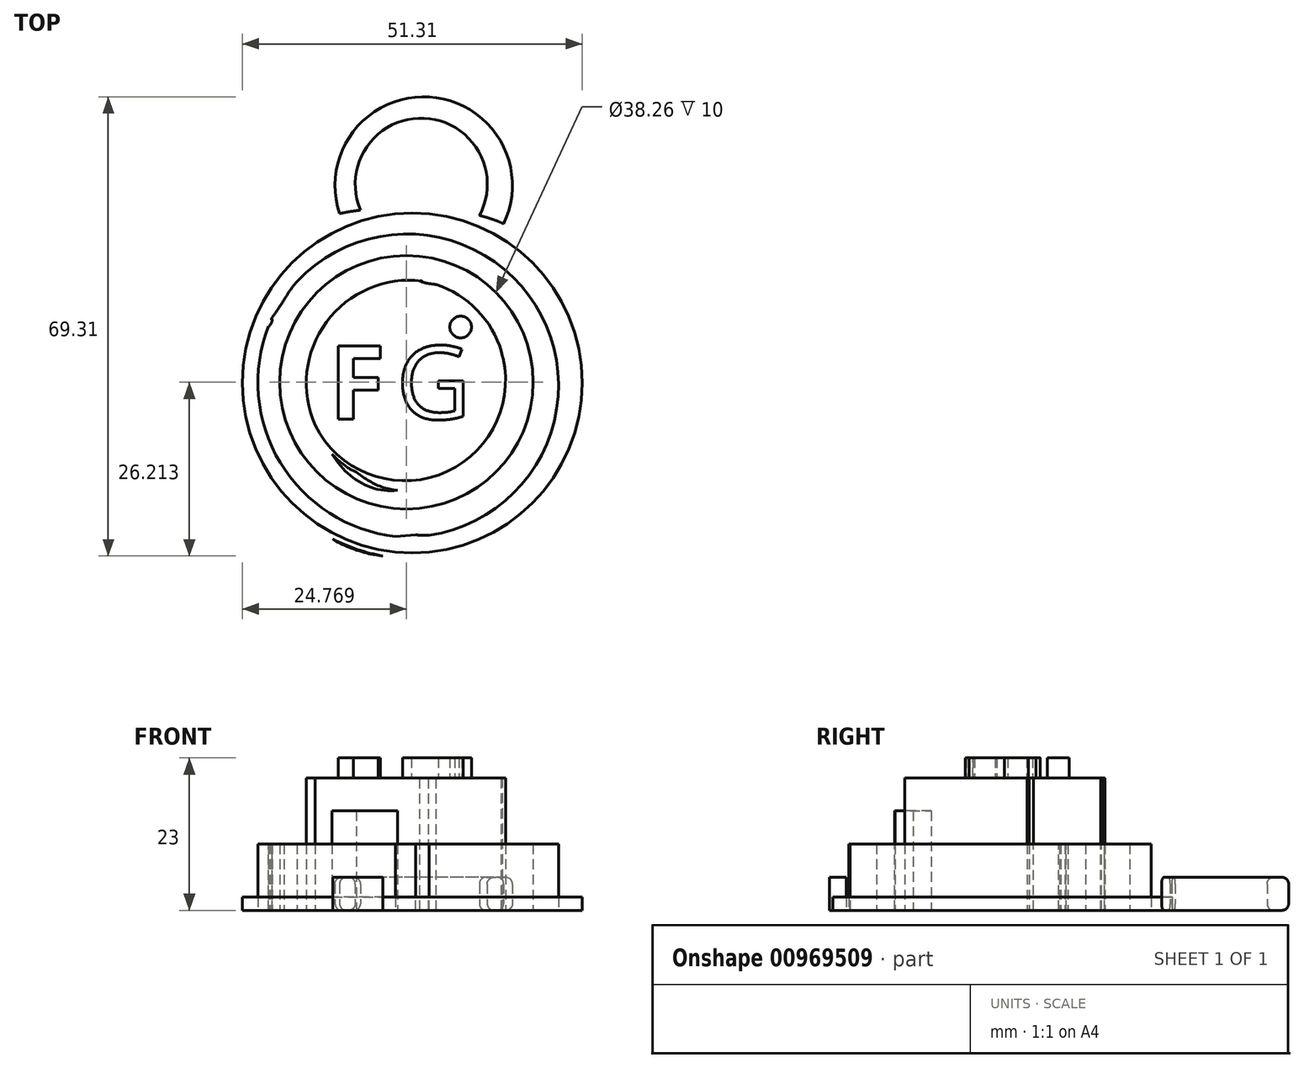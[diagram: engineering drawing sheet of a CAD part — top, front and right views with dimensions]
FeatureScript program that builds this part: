
annotation { "Feature Type Name" : "Feature", "Feature Type Description" : "" }
export const myFeature = defineFeature(function(context is Context, id is Id, definition is map)
    precondition{}
    {
        {
            var Q0;
            Q0=qCreatedBy(makeId("Top.planeOp"),FACE);
            var sketch = newSketch(context, id + "F0", { "sketchPlane" : qUnion([Q0])});
            skLineSegment(sketch, "E0", {"start": v(-44.03, -23.25) * mm, "end": v(-47.07, -23.48) * mm});
            skLineSegment(sketch, "E1", {"start": v(-47.07, -23.48) * mm, "end": v(-43.76, -23.38) * mm});
            skLineSegment(sketch, "E2", {"start": v(-0.42, -4.93) * mm, "end": v(0.75, -6.1) * mm});
            skLineSegment(sketch, "E3", {"start": v(0.75, -6.1) * mm, "end": v(0.2, -6.66) * mm});
            skLineSegment(sketch, "E4", {"start": v(0.2, -6.66) * mm, "end": v(-0.35, -7.2) * mm});
            skLineSegment(sketch, "E5", {"start": v(-0.35, -7.2) * mm, "end": v(-1.3, -6.23) * mm});
            skLineSegment(sketch, "E6", {"start": v(-5.27, -11.6) * mm, "end": v(-5.27, -10.95) * mm});
            skLineSegment(sketch, "E7", {"start": v(-5.27, -10.95) * mm, "end": v(-1.83, -10.95) * mm});
            skLineSegment(sketch, "E8", {"start": v(-1.83, -10.95) * mm, "end": v(1.61, -10.95) * mm});
            skLineSegment(sketch, "E9", {"start": v(1.61, -10.95) * mm, "end": v(1.53, -12.4) * mm});
            skLineSegment(sketch, "E10", {"start": v(34.95, -9.23) * mm, "end": v(34.95, -3.27) * mm});
            skLineSegment(sketch, "E11", {"start": v(34.95, -3.27) * mm, "end": v(35.66, -3.2) * mm});
            skLineSegment(sketch, "E12", {"start": v(35.66, -3.2) * mm, "end": v(36.37, -3.1) * mm});
            skLineSegment(sketch, "E13", {"start": v(36.37, -3.1) * mm, "end": v(36.45, -9.14) * mm});
            skLineSegment(sketch, "E14", {"start": v(44.6, -9.4) * mm, "end": v(44.74, -3.27) * mm});
            skLineSegment(sketch, "E15", {"start": v(44.74, -3.27) * mm, "end": v(45.47, -3.19) * mm});
            skLineSegment(sketch, "E16", {"start": v(45.47, -3.19) * mm, "end": v(46.2, -3.1) * mm});
            skLineSegment(sketch, "E17", {"start": v(46.2, -3.1) * mm, "end": v(46.18, -9.01) * mm});
            skLineSegment(sketch, "E18", {"start": v(4.45, -10.68) * mm, "end": v(4.52, -3.27) * mm});
            skLineSegment(sketch, "E19", {"start": v(4.52, -3.27) * mm, "end": v(5.85, -3.19) * mm});
            skLineSegment(sketch, "E20", {"start": v(9.42, -11.31) * mm, "end": v(8.63, -11.48) * mm});
            skLineSegment(sketch, "E21", {"start": v(8.63, -11.48) * mm, "end": v(11.3, -15.05) * mm});
            skLineSegment(sketch, "E22", {"start": v(11.3, -15.05) * mm, "end": v(13.95, -18.62) * mm});
            skLineSegment(sketch, "E23", {"start": v(13.95, -18.62) * mm, "end": v(13.08, -18.7) * mm});
            skLineSegment(sketch, "E24", {"start": v(5.98, -15.05) * mm, "end": v(5.98, -18.75) * mm});
            skLineSegment(sketch, "E25", {"start": v(5.98, -18.75) * mm, "end": v(5.3, -18.75) * mm});
            skLineSegment(sketch, "E26", {"start": v(7.18, -4.46) * mm, "end": v(5.98, -4.46) * mm});
            skLineSegment(sketch, "E27", {"start": v(5.98, -4.46) * mm, "end": v(5.98, -7.27) * mm});
            skLineSegment(sketch, "E28", {"start": v(5.98, -7.27) * mm, "end": v(5.98, -10.08) * mm});
            skLineSegment(sketch, "E29", {"start": v(5.98, -10.08) * mm, "end": v(7.86, -9.97) * mm});
            skLineSegment(sketch, "E30", {"start": v(49.96, -11.01) * mm, "end": v(50.03, -3.27) * mm});
            skLineSegment(sketch, "E31", {"start": v(50.03, -3.27) * mm, "end": v(51.62, -3.19) * mm});
            skLineSegment(sketch, "E32", {"start": v(52.88, -11.87) * mm, "end": v(51.49, -11.87) * mm});
            skLineSegment(sketch, "E33", {"start": v(51.49, -11.87) * mm, "end": v(51.49, -15.31) * mm});
            skLineSegment(sketch, "E34", {"start": v(51.49, -15.31) * mm, "end": v(51.49, -18.75) * mm});
            skLineSegment(sketch, "E35", {"start": v(51.49, -18.75) * mm, "end": v(50.69, -18.75) * mm});
            skLineSegment(sketch, "E36", {"start": v(50.69, -18.75) * mm, "end": v(49.9, -18.75) * mm});
            skLineSegment(sketch, "E37", {"start": v(49.9, -18.75) * mm, "end": v(49.96, -11.01) * mm});
            skLineSegment(sketch, "E38", {"start": v(52.61, -4.47) * mm, "end": v(51.49, -4.46) * mm});
            skLineSegment(sketch, "E39", {"start": v(51.49, -4.46) * mm, "end": v(51.49, -7.5) * mm});
            skLineSegment(sketch, "E40", {"start": v(-2.62, 13.4) * mm, "end": v(-2.62, 19.22) * mm});
            skLineSegment(sketch, "E41", {"start": v(-2.62, 19.22) * mm, "end": v(-1.38, 19.3) * mm});
            skLineSegment(sketch, "E42", {"start": v(-1.38, 19.3) * mm, "end": v(-0.14, 19.38) * mm});
            skLineSegment(sketch, "E43", {"start": v(-0.14, 19.38) * mm, "end": v(-0.06, 13.74) * mm});
            skLineSegment(sketch, "E44", {"start": v(7.57, 13.53) * mm, "end": v(7.7, 19.22) * mm});
            skLineSegment(sketch, "E45", {"start": v(7.7, 19.22) * mm, "end": v(8.89, 19.22) * mm});
            skLineSegment(sketch, "E46", {"start": v(8.89, 19.22) * mm, "end": v(10.08, 19.22) * mm});
            skLineSegment(sketch, "E47", {"start": v(10.08, 19.22) * mm, "end": v(10.08, 13.4) * mm});
            skLineSegment(sketch, "E48", {"start": v(1.1, 3.6) * mm, "end": v(1.1, 3.6) * mm});
            skLineSegment(sketch, "E49", {"start": v(22.7, 13.81) * mm, "end": v(22.78, 19.22) * mm});
            skLineSegment(sketch, "E50", {"start": v(22.78, 19.22) * mm, "end": v(23.97, 19.22) * mm});
            skLineSegment(sketch, "E51", {"start": v(23.97, 19.22) * mm, "end": v(25.16, 19.22) * mm});
            skLineSegment(sketch, "E52", {"start": v(25.16, 19.22) * mm, "end": v(25.3, 13.53) * mm});
            skLineSegment(sketch, "E53", {"start": v(32.92, 13.86) * mm, "end": v(33.01, 19.35) * mm});
            skLineSegment(sketch, "E54", {"start": v(33.01, 19.35) * mm, "end": v(34.18, 19.35) * mm});
            skLineSegment(sketch, "E55", {"start": v(34.18, 19.35) * mm, "end": v(35.35, 19.35) * mm});
            skLineSegment(sketch, "E56", {"start": v(35.35, 19.35) * mm, "end": v(35.35, 13.32) * mm});
            skLineSegment(sketch, "E57", {"start": v(-13.27, 11.48) * mm, "end": v(-13.2, 19.22) * mm});
            skLineSegment(sketch, "E58", {"start": v(-13.2, 19.22) * mm, "end": v(-8.97, 19.22) * mm});
            skLineSegment(sketch, "E59", {"start": v(-8.97, 19.22) * mm, "end": v(-4.74, 19.22) * mm});
            skLineSegment(sketch, "E60", {"start": v(-4.74, 19.22) * mm, "end": v(-4.66, 18.1) * mm});
            skLineSegment(sketch, "E61", {"start": v(-4.66, 18.1) * mm, "end": v(-4.57, 16.97) * mm});
            skLineSegment(sketch, "E62", {"start": v(-4.57, 16.97) * mm, "end": v(-7.63, 16.97) * mm});
            skLineSegment(sketch, "E63", {"start": v(-7.63, 16.97) * mm, "end": v(-10.69, 16.97) * mm});
            skLineSegment(sketch, "E64", {"start": v(-10.69, 16.97) * mm, "end": v(-10.69, 15.12) * mm});
            skLineSegment(sketch, "E65", {"start": v(-10.69, 15.12) * mm, "end": v(-10.69, 13.26) * mm});
            skLineSegment(sketch, "E66", {"start": v(-10.69, 13.26) * mm, "end": v(-7.65, 13.26) * mm});
            skLineSegment(sketch, "E67", {"start": v(-7.65, 13.26) * mm, "end": v(-4.6, 13.26) * mm});
            skLineSegment(sketch, "E68", {"start": v(-4.6, 13.26) * mm, "end": v(-4.6, 12.07) * mm});
            skLineSegment(sketch, "E69", {"start": v(-4.6, 12.07) * mm, "end": v(-4.6, 10.88) * mm});
            skLineSegment(sketch, "E70", {"start": v(-4.6, 10.88) * mm, "end": v(-7.65, 10.88) * mm});
            skLineSegment(sketch, "E71", {"start": v(-7.65, 10.88) * mm, "end": v(-10.69, 10.88) * mm});
            skLineSegment(sketch, "E72", {"start": v(-10.69, 10.88) * mm, "end": v(-10.69, 7.31) * mm});
            skLineSegment(sketch, "E73", {"start": v(-10.69, 7.31) * mm, "end": v(-10.69, 3.74) * mm});
            skLineSegment(sketch, "E74", {"start": v(-10.69, 3.74) * mm, "end": v(-12.02, 3.74) * mm});
            skLineSegment(sketch, "E75", {"start": v(-12.02, 3.74) * mm, "end": v(-13.34, 3.74) * mm});
            skLineSegment(sketch, "E76", {"start": v(-13.34, 3.74) * mm, "end": v(-13.27, 11.48) * mm});
            skLineSegment(sketch, "E77", {"start": v(14.99, 10.29) * mm, "end": v(15.01, 16.84) * mm});
            skLineSegment(sketch, "E78", {"start": v(15.01, 16.84) * mm, "end": v(13, 16.91) * mm});
            skLineSegment(sketch, "E79", {"start": v(13, 16.91) * mm, "end": v(10.98, 17) * mm});
            skLineSegment(sketch, "E80", {"start": v(10.98, 17) * mm, "end": v(11.06, 18.1) * mm});
            skLineSegment(sketch, "E81", {"start": v(11.06, 18.1) * mm, "end": v(11.14, 19.22) * mm});
            skLineSegment(sketch, "E82", {"start": v(11.14, 19.22) * mm, "end": v(16.43, 19.22) * mm});
            skLineSegment(sketch, "E83", {"start": v(16.43, 19.22) * mm, "end": v(21.72, 19.22) * mm});
            skLineSegment(sketch, "E84", {"start": v(21.72, 19.22) * mm, "end": v(21.8, 18.1) * mm});
            skLineSegment(sketch, "E85", {"start": v(21.8, 18.1) * mm, "end": v(21.88, 17) * mm});
            skLineSegment(sketch, "E86", {"start": v(21.88, 17) * mm, "end": v(19.82, 16.91) * mm});
            skLineSegment(sketch, "E87", {"start": v(19.82, 16.91) * mm, "end": v(17.75, 16.84) * mm});
            skLineSegment(sketch, "E88", {"start": v(17.75, 16.84) * mm, "end": v(17.75, 10.29) * mm});
            skLineSegment(sketch, "E89", {"start": v(17.75, 10.29) * mm, "end": v(17.75, 3.74) * mm});
            skLineSegment(sketch, "E90", {"start": v(17.75, 3.74) * mm, "end": v(16.36, 3.74) * mm});
            skLineSegment(sketch, "E91", {"start": v(16.36, 3.74) * mm, "end": v(14.96, 3.74) * mm});
            skLineSegment(sketch, "E92", {"start": v(14.96, 3.74) * mm, "end": v(14.99, 10.29) * mm});
            skLineSegment(sketch, "E93", {"start": v(38.06, 11.48) * mm, "end": v(38.13, 19.22) * mm});
            skLineSegment(sketch, "E94", {"start": v(38.13, 19.22) * mm, "end": v(41.1, 19.18) * mm});
            skLineSegment(sketch, "E95", {"start": v(44.73, 11.04) * mm, "end": v(43.66, 10.55) * mm});
            skLineSegment(sketch, "E96", {"start": v(43.66, 10.55) * mm, "end": v(46.05, 7.29) * mm});
            skLineSegment(sketch, "E97", {"start": v(63.29, 4.6) * mm, "end": v(63.67, 3.74) * mm});
            skLineSegment(sketch, "E98", {"start": v(63.67, 3.74) * mm, "end": v(62.27, 3.74) * mm});
            skLineSegment(sketch, "E99", {"start": v(62.27, 3.74) * mm, "end": v(60.88, 3.74) * mm});
            skLineSegment(sketch, "E100", {"start": v(60.88, 3.74) * mm, "end": v(60.06, 5.66) * mm});
            skLineSegment(sketch, "E101", {"start": v(60.06, 5.66) * mm, "end": v(59.24, 7.57) * mm});
            skLineSegment(sketch, "E102", {"start": v(59.24, 7.57) * mm, "end": v(56.22, 7.57) * mm});
            skLineSegment(sketch, "E103", {"start": v(56.22, 7.57) * mm, "end": v(53.2, 7.57) * mm});
            skLineSegment(sketch, "E104", {"start": v(53.2, 7.57) * mm, "end": v(52.75, 6.66) * mm});
            skLineSegment(sketch, "E105", {"start": v(51.9, 4.74) * mm, "end": v(51.5, 3.74) * mm});
            skLineSegment(sketch, "E106", {"start": v(51.5, 3.74) * mm, "end": v(48.6, 3.74) * mm});
            skLineSegment(sketch, "E107", {"start": v(48.6, 3.74) * mm, "end": v(45.7, 3.74) * mm});
            skLineSegment(sketch, "E108", {"start": v(45.7, 3.74) * mm, "end": v(43.43, 6.9) * mm});
            skLineSegment(sketch, "E109", {"start": v(40.64, 7.06) * mm, "end": v(40.64, 3.74) * mm});
            skLineSegment(sketch, "E110", {"start": v(40.64, 3.74) * mm, "end": v(39.31, 3.74) * mm});
            skLineSegment(sketch, "E111", {"start": v(39.31, 3.74) * mm, "end": v(37.99, 3.74) * mm});
            skLineSegment(sketch, "E112", {"start": v(37.99, 3.74) * mm, "end": v(38.06, 11.48) * mm});
            skLineSegment(sketch, "E113", {"start": v(42.1, 16.79) * mm, "end": v(40.77, 16.84) * mm});
            skLineSegment(sketch, "E114", {"start": v(40.77, 16.84) * mm, "end": v(40.7, 14.78) * mm});
            skLineSegment(sketch, "E115", {"start": v(40.7, 14.78) * mm, "end": v(40.62, 12.73) * mm});
            skLineSegment(sketch, "E116", {"start": v(40.62, 12.73) * mm, "end": v(41.95, 12.73) * mm});
            skFitSpline(sketch, "E117", {"points": [v(-48.97, -26.41) * mm, v(-51.63, -25.94) * mm, v(-55.3, -24.57) * mm, v(-57.59, -23.21) * mm]});
            skFitSpline(sketch, "E118", {"points": [v(-57.59, -23.21) * mm, v(-63.3, -19.81) * mm, v(-66.86, -15.56) * mm, v(-69.4, -9.15) * mm]});
            skFitSpline(sketch, "E119", {"points": [v(-69.4, -9.15) * mm, v(-71.48, -3.92) * mm, v(-71.54, 3.34) * mm, v(-69.55, 8.65) * mm]});
            skFitSpline(sketch, "E120", {"points": [v(-69.56, 8.67) * mm, v(-66.12, 17.83) * mm, v(-58.94, 24.16) * mm, v(-49.87, 26.04) * mm]});
            skFitSpline(sketch, "E121", {"points": [v(-49.86, 26.02) * mm, v(-46.19, 26.78) * mm, v(-40.37, 26.59) * mm, v(-37.07, 25.6) * mm]});
            skFitSpline(sketch, "E122", {"points": [v(-37.07, 25.6) * mm, v(-30.64, 23.67) * mm, v(-25.03, 19.32) * mm, v(-21.64, 13.64) * mm]});
            skFitSpline(sketch, "E123", {"points": [v(-21.64, 13.64) * mm, v(-17.98, 7.51) * mm, v(-16.93, 0.08) * mm, v(-18.72, -6.9) * mm]});
            skFitSpline(sketch, "E124", {"points": [v(-18.72, -6.9) * mm, v(-21.07, -16.02) * mm, v(-28.59, -23.55) * mm, v(-37.68, -25.92) * mm]});
            skFitSpline(sketch, "E125", {"points": [v(-37.68, -25.92) * mm, v(-40.2, -26.57) * mm, v(-46.51, -26.85) * mm, v(-48.97, -26.41) * mm]});
            skFitSpline(sketch, "E126", {"points": [v(-38.2, -22.63) * mm, v(-35.14, -21.72) * mm, v(-33.7, -21.08) * mm, v(-31.51, -19.6) * mm]});
            skFitSpline(sketch, "E127", {"points": [v(-31.51, -19.6) * mm, v(-26.64, -16.35) * mm, v(-23.18, -11.38) * mm, v(-21.75, -5.6) * mm]});
            skFitSpline(sketch, "E128", {"points": [v(-21.75, -5.6) * mm, v(-20.9, -2.13) * mm, v(-20.94, 2.46) * mm, v(-21.88, 5.9) * mm]});
            skFitSpline(sketch, "E129", {"points": [v(-21.88, 5.9) * mm, v(-23.68, 12.54) * mm, v(-28.15, 18.04) * mm, v(-34.12, 20.95) * mm]});
            skFitSpline(sketch, "E130", {"points": [v(-34.12, 20.95) * mm, v(-39.89, 23.76) * mm, v(-46.96, 24.05) * mm, v(-53.02, 21.71) * mm]});
            skFitSpline(sketch, "E131", {"points": [v(-53.02, 21.71) * mm, v(-57.82, 19.87) * mm, v(-62.76, 15.41) * mm, v(-65.06, 10.88) * mm]});
            skFitSpline(sketch, "E132", {"points": [v(-65.06, 10.88) * mm, v(-65.7, 9.62) * mm, v(-65.47, 9.88) * mm, v(-63.9, 12.23) * mm]});
            skFitSpline(sketch, "E133", {"points": [v(-63.9, 12.23) * mm, v(-62.4, 14.5) * mm, v(-59.48, 17.39) * mm, v(-57.14, 18.93) * mm]});
            skFitSpline(sketch, "E134", {"points": [v(-57.14, 18.93) * mm, v(-55.36, 20.11) * mm, v(-52.56, 21.26) * mm, v(-49.92, 21.9) * mm]});
            skFitSpline(sketch, "E135", {"points": [v(-49.92, 21.9) * mm, v(-47.26, 22.55) * mm, v(-42.13, 22.48) * mm, v(-39.4, 21.75) * mm]});
            skFitSpline(sketch, "E136", {"points": [v(-39.4, 21.75) * mm, v(-31.8, 19.74) * mm, v(-25.84, 14.14) * mm, v(-23.33, 6.65) * mm]});
            skFitSpline(sketch, "E137", {"points": [v(-23.33, 6.65) * mm, v(-22.52, 4.24) * mm, v(-22.49, 3.96) * mm, v(-22.48, -0.23) * mm]});
            skFitSpline(sketch, "E138", {"points": [v(-22.48, -0.23) * mm, v(-22.46, -5.24) * mm, v(-22.86, -7.13) * mm, v(-24.7, -10.8) * mm]});
            skFitSpline(sketch, "E139", {"points": [v(-24.7, -10.8) * mm, v(-28.37, -18.09) * mm, v(-35.4, -22.62) * mm, v(-44.03, -23.25) * mm]});
            skFitSpline(sketch, "E140", {"points": [v(-43.76, -23.38) * mm, v(-41.2, -23.31) * mm, v(-39.94, -23.14) * mm, v(-38.2, -22.63) * mm]});
            skFitSpline(sketch, "E141", {"points": [v(-41.15, -15.54) * mm, v(-37.63, -14.7) * mm, v(-33.69, -11.85) * mm, v(-31.89, -8.86) * mm]});
            skFitSpline(sketch, "E142", {"points": [v(-31.89, -8.86) * mm, v(-30.14, -5.94) * mm, v(-29.65, -4.17) * mm, v(-29.63, -0.63) * mm]});
            skFitSpline(sketch, "E143", {"points": [v(-29.63, -0.63) * mm, v(-29.61, 2.06) * mm, v(-29.7, 2.85) * mm, v(-30.25, 4.52) * mm]});
            skFitSpline(sketch, "E144", {"points": [v(-30.25, 4.52) * mm, v(-31.54, 8.44) * mm, v(-34.55, 11.9) * mm, v(-38.14, 13.6) * mm]});
            skFitSpline(sketch, "E145", {"points": [v(-38.14, 13.6) * mm, v(-39.89, 14.42) * mm, v(-42.23, 15.12) * mm, v(-43.1, 15.1) * mm]});
            skFitSpline(sketch, "E146", {"points": [v(-43.1, 15.1) * mm, v(-43.4, 15.08) * mm, v(-42.93, 14.9) * mm, v(-42.08, 14.7) * mm]});
            skFitSpline(sketch, "E147", {"points": [v(-42.08, 14.7) * mm, v(-36.92, 13.45) * mm, v(-32.57, 9.17) * mm, v(-30.96, 3.76) * mm]});
            skFitSpline(sketch, "E148", {"points": [v(-30.96, 3.76) * mm, v(-30.42, 1.93) * mm, v(-30.4, -1.75) * mm, v(-30.94, -3.79) * mm]});
            skFitSpline(sketch, "E149", {"points": [v(-30.94, -3.79) * mm, v(-31.46, -5.77) * mm, v(-32.89, -8.48) * mm, v(-34.25, -10.07) * mm]});
            skFitSpline(sketch, "E150", {"points": [v(-34.25, -10.07) * mm, v(-35.7, -11.76) * mm, v(-38.9, -13.86) * mm, v(-41.05, -14.52) * mm]});
            skFitSpline(sketch, "E151", {"points": [v(-41.05, -14.52) * mm, v(-47.68, -16.57) * mm, v(-53.9, -14.29) * mm, v(-58.4, -8.15) * mm]});
            skFitSpline(sketch, "E152", {"points": [v(-58.4, -8.15) * mm, v(-58.85, -7.53) * mm, v(-58.85, -7.54) * mm, v(-58.4, -8.41) * mm]});
            skFitSpline(sketch, "E153", {"points": [v(-58.4, -8.41) * mm, v(-57.6, -9.92) * mm, v(-54.78, -12.73) * mm, v(-52.99, -13.8) * mm]});
            skFitSpline(sketch, "E154", {"points": [v(-52.99, -13.8) * mm, v(-49.48, -15.88) * mm, v(-45.2, -16.5) * mm, v(-41.15, -15.54) * mm]});
            skFitSpline(sketch, "E155", {"points": [v(-65.73, 9.16) * mm, v(-65.73, 9.3) * mm, v(-65.85, 9.25) * mm, v(-65.99, 9.03) * mm]});
            skFitSpline(sketch, "E156", {"points": [v(-65.99, 9.03) * mm, v(-66.13, 8.81) * mm, v(-66.24, 8.51) * mm, v(-66.24, 8.37) * mm]});
            skFitSpline(sketch, "E157", {"points": [v(-66.24, 8.37) * mm, v(-66.24, 8.22) * mm, v(-66.13, 8.28) * mm, v(-65.99, 8.5) * mm]});
            skFitSpline(sketch, "E158", {"points": [v(-65.99, 8.5) * mm, v(-65.85, 8.72) * mm, v(-65.73, 9.02) * mm, v(-65.73, 9.16) * mm]});
            skFitSpline(sketch, "E159", {"points": [v(-7.85, -19) * mm, v(-10.55, -18.33) * mm, v(-12.78, -16.26) * mm, v(-13.5, -13.77) * mm]});
            skFitSpline(sketch, "E160", {"points": [v(-13.5, -13.77) * mm, v(-14.05, -11.9) * mm, v(-13.89, -9) * mm, v(-13.15, -7.37) * mm]});
            skFitSpline(sketch, "E161", {"points": [v(-13.15, -7.37) * mm, v(-11.9, -4.6) * mm, v(-9.18, -2.88) * mm, v(-6.04, -2.88) * mm]});
            skFitSpline(sketch, "E162", {"points": [v(-6.04, -2.88) * mm, v(-3.52, -2.88) * mm, v(-1.87, -3.48) * mm, v(-0.42, -4.93) * mm]});
            skFitSpline(sketch, "E163", {"points": [v(-1.3, -6.23) * mm, v(-2.48, -5.02) * mm, v(-3.34, -4.57) * mm, v(-4.93, -4.33) * mm]});
            skFitSpline(sketch, "E164", {"points": [v(-4.93, -4.33) * mm, v(-6.78, -4.05) * mm, v(-8.6, -4.58) * mm, v(-10, -5.82) * mm]});
            skFitSpline(sketch, "E165", {"points": [v(-10, -5.82) * mm, v(-11.52, -7.15) * mm, v(-12.15, -8.75) * mm, v(-12.13, -11.22) * mm]});
            skFitSpline(sketch, "E166", {"points": [v(-12.13, -11.22) * mm, v(-12.11, -14.87) * mm, v(-9.8, -17.42) * mm, v(-6.32, -17.65) * mm]});
            skFitSpline(sketch, "E167", {"points": [v(-6.32, -17.65) * mm, v(-4.4, -17.77) * mm, v(-3.08, -17.4) * mm, v(-1.91, -16.42) * mm]});
            skFitSpline(sketch, "E168", {"points": [v(-1.91, -16.42) * mm, v(-1.03, -15.68) * mm, v(-0.12, -13.96) * mm, v(-0.11, -13) * mm]});
            skFitSpline(sketch, "E169", {"points": [v(-0.11, -13) * mm, v(-0.1, -12.45) * mm, v(-0.22, -12.42) * mm, v(-2.69, -12.34) * mm]});
            skFitSpline(sketch, "E170", {"points": [v(-2.69, -12.34) * mm, v(-5.24, -12.27) * mm, v(-5.27, -12.26) * mm, v(-5.27, -11.6) * mm]});
            skFitSpline(sketch, "E171", {"points": [v(1.53, -12.4) * mm, v(1.39, -15.08) * mm, v(0, -17.2) * mm, v(-2.3, -18.34) * mm]});
            skFitSpline(sketch, "E172", {"points": [v(-2.3, -18.34) * mm, v(-3.85, -19.1) * mm, v(-6.31, -19.4) * mm, v(-7.85, -19) * mm]});
            skFitSpline(sketch, "E173", {"points": [v(21.57, -18.93) * mm, v(19.9, -18.46) * mm, v(18.03, -17.32) * mm, v(17.26, -16.3) * mm]});
            skFitSpline(sketch, "E174", {"points": [v(17.26, -16.3) * mm, v(15.86, -14.42) * mm, v(15.4, -13.16) * mm, v(15.39, -11.08) * mm]});
            skFitSpline(sketch, "E175", {"points": [v(15.39, -11.08) * mm, v(15.36, -7.62) * mm, v(16.98, -5.1) * mm, v(20.2, -3.6) * mm]});
            skFitSpline(sketch, "E176", {"points": [v(20.2, -3.6) * mm, v(21.7, -2.9) * mm, v(22.08, -2.83) * mm, v(23.91, -2.93) * mm]});
            skFitSpline(sketch, "E177", {"points": [v(23.91, -2.93) * mm, v(26.33, -3.06) * mm, v(27.95, -3.74) * mm, v(29.5, -5.3) * mm]});
            skFitSpline(sketch, "E178", {"points": [v(29.5, -5.3) * mm, v(33.43, -9.22) * mm, v(32.34, -15.77) * mm, v(27.36, -18.2) * mm]});
            skFitSpline(sketch, "E179", {"points": [v(27.36, -18.2) * mm, v(25.4, -19.15) * mm, v(23.3, -19.42) * mm, v(21.57, -18.93) * mm]});
            skFitSpline(sketch, "E180", {"points": [v(26.82, -16.89) * mm, v(29.99, -15.07) * mm, v(31.18, -11.15) * mm, v(29.54, -7.93) * mm]});
            skFitSpline(sketch, "E181", {"points": [v(29.54, -7.93) * mm, v(28.86, -6.6) * mm, v(26.92, -4.9) * mm, v(25.6, -4.51) * mm]});
            skFitSpline(sketch, "E182", {"points": [v(25.6, -4.51) * mm, v(23.3, -3.82) * mm, v(21.1, -4.29) * mm, v(19.31, -5.87) * mm]});
            skFitSpline(sketch, "E183", {"points": [v(19.31, -5.87) * mm, v(17.15, -7.77) * mm, v(16.4, -10.27) * mm, v(17.18, -12.96) * mm]});
            skFitSpline(sketch, "E184", {"points": [v(17.18, -12.96) * mm, v(18.05, -15.95) * mm, v(20.37, -17.66) * mm, v(23.57, -17.68) * mm]});
            skFitSpline(sketch, "E185", {"points": [v(23.57, -17.68) * mm, v(25.16, -17.69) * mm, v(25.62, -17.57) * mm, v(26.82, -16.89) * mm]});
            skFitSpline(sketch, "E186", {"points": [v(38.88, -19.04) * mm, v(37.4, -18.66) * mm, v(36.2, -17.73) * mm, v(35.56, -16.43) * mm]});
            skFitSpline(sketch, "E187", {"points": [v(35.56, -16.43) * mm, v(34.98, -15.23) * mm, v(34.95, -14.92) * mm, v(34.95, -9.23) * mm]});
            skFitSpline(sketch, "E188", {"points": [v(36.45, -9.14) * mm, v(36.53, -14.3) * mm, v(36.6, -15.3) * mm, v(37, -16.03) * mm]});
            skFitSpline(sketch, "E189", {"points": [v(37, -16.03) * mm, v(37.64, -17.2) * mm, v(38.72, -17.7) * mm, v(40.56, -17.69) * mm]});
            skFitSpline(sketch, "E190", {"points": [v(40.56, -17.69) * mm, v(42.32, -17.68) * mm, v(43.13, -17.34) * mm, v(43.92, -16.29) * mm]});
            skFitSpline(sketch, "E191", {"points": [v(43.92, -16.29) * mm, v(44.44, -15.6) * mm, v(44.49, -15.1) * mm, v(44.6, -9.4) * mm]});
            skFitSpline(sketch, "E192", {"points": [v(46.18, -9.01) * mm, v(46.17, -15.16) * mm, v(46, -16.32) * mm, v(44.96, -17.47) * mm]});
            skFitSpline(sketch, "E193", {"points": [v(44.96, -17.47) * mm, v(43.8, -18.77) * mm, v(40.82, -19.54) * mm, v(38.88, -19.04) * mm]});
            skFitSpline(sketch, "E194", {"points": [v(4.51, -18.42) * mm, v(4.44, -18.23) * mm, v(4.41, -14.75) * mm, v(4.45, -10.68) * mm]});
            skFitSpline(sketch, "E195", {"points": [v(5.85, -3.19) * mm, v(9, -2.98) * mm, v(11.26, -3.77) * mm, v(12.01, -5.33) * mm]});
            skFitSpline(sketch, "E196", {"points": [v(12.01, -5.33) * mm, v(12.5, -6.34) * mm, v(12.46, -8.46) * mm, v(11.95, -9.45) * mm]});
            skFitSpline(sketch, "E197", {"points": [v(11.95, -9.45) * mm, v(11.46, -10.4) * mm, v(10.54, -11.08) * mm, v(9.42, -11.31) * mm]});
            skFitSpline(sketch, "E198", {"points": [v(13.08, -18.7) * mm, v(12.48, -18.77) * mm, v(12.12, -18.65) * mm, v(11.87, -18.3) * mm]});
            skFitSpline(sketch, "E199", {"points": [v(11.87, -18.3) * mm, v(8.9, -14.16) * mm, v(6.68, -11.34) * mm, v(6.37, -11.34) * mm]});
            skFitSpline(sketch, "E200", {"points": [v(6.37, -11.34) * mm, v(6.04, -11.34) * mm, v(5.98, -11.98) * mm, v(5.98, -15.05) * mm]});
            skFitSpline(sketch, "E201", {"points": [v(5.3, -18.75) * mm, v(4.94, -18.75) * mm, v(4.58, -18.6) * mm, v(4.51, -18.42) * mm]});
            skFitSpline(sketch, "E202", {"points": [v(10.24, -9.25) * mm, v(10.8, -8.56) * mm, v(10.92, -6.62) * mm, v(10.46, -5.75) * mm]});
            skFitSpline(sketch, "E203", {"points": [v(10.46, -5.75) * mm, v(10.07, -5.02) * mm, v(8.64, -4.46) * mm, v(7.18, -4.46) * mm]});
            skFitSpline(sketch, "E204", {"points": [v(7.86, -9.97) * mm, v(9.44, -9.88) * mm, v(9.83, -9.77) * mm, v(10.24, -9.25) * mm]});
            skFitSpline(sketch, "E205", {"points": [v(51.62, -3.19) * mm, v(52.5, -3.14) * mm, v(53.86, -3.18) * mm, v(54.66, -3.28) * mm]});
            skFitSpline(sketch, "E206", {"points": [v(54.66, -3.28) * mm, v(55.9, -3.43) * mm, v(56.27, -3.62) * mm, v(57.1, -4.48) * mm]});
            skFitSpline(sketch, "E207", {"points": [v(57.1, -4.48) * mm, v(58.22, -5.67) * mm, v(58.58, -7.19) * mm, v(58.13, -8.86) * mm]});
            skFitSpline(sketch, "E208", {"points": [v(58.13, -8.86) * mm, v(57.6, -10.84) * mm, v(55.8, -11.87) * mm, v(52.88, -11.87) * mm]});
            skFitSpline(sketch, "E209", {"points": [v(53.99, -10.29) * mm, v(56.05, -9.95) * mm, v(56.62, -9.39) * mm, v(56.62, -7.68) * mm]});
            skFitSpline(sketch, "E210", {"points": [v(56.62, -7.68) * mm, v(56.62, -5.4) * mm, v(55.44, -4.47) * mm, v(52.61, -4.47) * mm]});
            skFitSpline(sketch, "E211", {"points": [v(51.49, -7.5) * mm, v(51.49, -10.96) * mm, v(51.28, -10.73) * mm, v(53.99, -10.29) * mm]});
            skFitSpline(sketch, "E212", {"points": [v(1.1, 3.6) * mm, v(-0.47, 4.16) * mm, v(-1.23, 4.82) * mm, v(-1.96, 6.27) * mm]});
            skFitSpline(sketch, "E213", {"points": [v(-1.96, 6.27) * mm, v(-2.6, 7.54) * mm, v(-2.62, 7.71) * mm, v(-2.62, 13.4) * mm]});
            skFitSpline(sketch, "E214", {"points": [v(-0.06, 13.74) * mm, v(0.04, 7.33) * mm, v(0.2, 6.74) * mm, v(2.07, 6) * mm]});
            skFitSpline(sketch, "E215", {"points": [v(2.07, 6) * mm, v(3.35, 5.48) * mm, v(4.12, 5.48) * mm, v(5.43, 6) * mm]});
            skFitSpline(sketch, "E216", {"points": [v(5.43, 6) * mm, v(7.32, 6.77) * mm, v(7.42, 7.1) * mm, v(7.57, 13.53) * mm]});
            skFitSpline(sketch, "E217", {"points": [v(10.08, 13.4) * mm, v(10.08, 10.2) * mm, v(9.99, 7.24) * mm, v(9.87, 6.84) * mm]});
            skFitSpline(sketch, "E218", {"points": [v(9.87, 6.84) * mm, v(9.52, 5.55) * mm, v(7.9, 4.05) * mm, v(6.43, 3.6) * mm]});
            skFitSpline(sketch, "E219", {"points": [v(6.43, 3.6) * mm, v(4.77, 3.11) * mm, v(2.48, 3.11) * mm, v(1.1, 3.6) * mm]});
            skFitSpline(sketch, "E220", {"points": [v(26.38, 3.6) * mm, v(25.74, 3.8) * mm, v(24.82, 4.36) * mm, v(24.32, 4.84) * mm]});
            skFitSpline(sketch, "E221", {"points": [v(24.32, 4.84) * mm, v(22.86, 6.26) * mm, v(22.63, 7.56) * mm, v(22.7, 13.81) * mm]});
            skFitSpline(sketch, "E222", {"points": [v(25.3, 13.53) * mm, v(25.44, 7.04) * mm, v(25.53, 6.74) * mm, v(27.56, 5.97) * mm]});
            skFitSpline(sketch, "E223", {"points": [v(27.56, 5.97) * mm, v(28.92, 5.45) * mm, v(30.36, 5.59) * mm, v(31.37, 6.33) * mm]});
            skFitSpline(sketch, "E224", {"points": [v(31.37, 6.33) * mm, v(32.7, 7.31) * mm, v(32.83, 7.96) * mm, v(32.92, 13.86) * mm]});
            skFitSpline(sketch, "E225", {"points": [v(35.35, 13.32) * mm, v(35.35, 7.6) * mm, v(35.32, 7.23) * mm, v(34.75, 6.11) * mm]});
            skFitSpline(sketch, "E226", {"points": [v(34.75, 6.11) * mm, v(34.1, 4.83) * mm, v(32.92, 3.9) * mm, v(31.41, 3.48) * mm]});
            skFitSpline(sketch, "E227", {"points": [v(31.41, 3.48) * mm, v(30.1, 3.11) * mm, v(27.78, 3.17) * mm, v(26.38, 3.6) * mm]});
            skFitSpline(sketch, "E228", {"points": [v(41.1, 19.18) * mm, v(43.46, 19.15) * mm, v(44.23, 19.04) * mm, v(44.9, 18.65) * mm]});
            skFitSpline(sketch, "E229", {"points": [v(44.9, 18.65) * mm, v(46.28, 17.84) * mm, v(46.82, 16.9) * mm, v(46.93, 15.05) * mm]});
            skFitSpline(sketch, "E230", {"points": [v(46.93, 15.05) * mm, v(47.02, 13.65) * mm, v(46.94, 13.25) * mm, v(46.42, 12.47) * mm]});
            skFitSpline(sketch, "E231", {"points": [v(46.42, 12.47) * mm, v(46.08, 11.96) * mm, v(45.32, 11.32) * mm, v(44.73, 11.04) * mm]});
            skFitSpline(sketch, "E232", {"points": [v(46.05, 7.29) * mm, v(47.37, 5.5) * mm, v(48.5, 4.03) * mm, v(48.59, 4.02) * mm]});
            skFitSpline(sketch, "E233", {"points": [v(48.59, 4.02) * mm, v(48.78, 4) * mm, v(49.77, 6.01) * mm, v(52.54, 12.07) * mm]});
            skFitSpline(sketch, "E234", {"points": [v(52.54, 12.07) * mm, v(53.8, 14.84) * mm, v(55.14, 17.69) * mm, v(55.5, 18.4) * mm]});
            skFitSpline(sketch, "E235", {"points": [v(55.5, 18.4) * mm, v(56.18, 19.71) * mm, v(56.18, 19.71) * mm, v(56.52, 19.07) * mm]});
            skFitSpline(sketch, "E236", {"points": [v(56.52, 19.07) * mm, v(56.87, 18.43) * mm, v(62.55, 6.27) * mm, v(63.29, 4.6) * mm]});
            skFitSpline(sketch, "E237", {"points": [v(52.75, 6.66) * mm, v(52.5, 6.16) * mm, v(52.12, 5.3) * mm, v(51.9, 4.74) * mm]});
            skFitSpline(sketch, "E238", {"points": [v(43.43, 6.9) * mm, v(42.17, 8.64) * mm, v(41.04, 10.14) * mm, v(40.9, 10.23) * mm]});
            skFitSpline(sketch, "E239", {"points": [v(40.9, 10.23) * mm, v(40.74, 10.32) * mm, v(40.64, 9.14) * mm, v(40.64, 7.06) * mm]});
            skFitSpline(sketch, "E240", {"points": [v(58.1, 9.98) * mm, v(58.1, 10.06) * mm, v(57.76, 10.93) * mm, v(57.35, 11.9) * mm]});
            skFitSpline(sketch, "E241", {"points": [v(57.35, 11.9) * mm, v(56.93, 12.87) * mm, v(56.5, 13.9) * mm, v(56.4, 14.18) * mm]});
            skFitSpline(sketch, "E242", {"points": [v(56.4, 14.18) * mm, v(56.26, 14.58) * mm, v(56.01, 14.19) * mm, v(55.31, 12.46) * mm]});
            skFitSpline(sketch, "E243", {"points": [v(55.31, 12.46) * mm, v(54.82, 11.23) * mm, v(54.4, 10.13) * mm, v(54.4, 10.02) * mm]});
            skFitSpline(sketch, "E244", {"points": [v(54.4, 10.02) * mm, v(54.4, 9.91) * mm, v(55.23, 9.82) * mm, v(56.25, 9.82) * mm]});
            skFitSpline(sketch, "E245", {"points": [v(56.25, 9.82) * mm, v(57.27, 9.82) * mm, v(58.1, 9.9) * mm, v(58.1, 9.98) * mm]});
            skFitSpline(sketch, "E246", {"points": [v(43.81, 13.26) * mm, v(44.48, 13.93) * mm, v(44.5, 15.38) * mm, v(43.88, 16.16) * mm]});
            skFitSpline(sketch, "E247", {"points": [v(43.88, 16.16) * mm, v(43.52, 16.6) * mm, v(43.09, 16.75) * mm, v(42.1, 16.79) * mm]});
            skFitSpline(sketch, "E248", {"points": [v(41.95, 12.73) * mm, v(42.93, 12.73) * mm, v(43.43, 12.87) * mm, v(43.81, 13.26) * mm]});
            skFitSpline(sketch, "E249", {"points": [v(65.14, 19.6) * mm, v(61.89, 21.74) * mm, v(63.25, 26.62) * mm, v(67.1, 26.62) * mm]});
            skFitSpline(sketch, "E250", {"points": [v(67.1, 26.62) * mm, v(69.92, 26.62) * mm, v(71.89, 23.58) * mm, v(70.6, 21.2) * mm]});
            skFitSpline(sketch, "E251", {"points": [v(70.6, 21.2) * mm, v(69.5, 19.22) * mm, v(66.89, 18.44) * mm, v(65.14, 19.6) * mm]});
            skCircle(sketch, "E252", {"center": v(-45.65, 0.12) * mm, "radius": 15.19 * mm});
            skPoint(sketch, "E252.second.point", {"position": v(-32.39, -7.28) * mm});
            skCircle(sketch, "E253", {"center": v(-44.97, -0.39) * mm, "radius": 15.59 * mm});
            skPoint(sketch, "E253.third.point", {"position": v(-57.19, -10.07) * mm});
            skCircle(sketch, "E254", {"center": v(-45.43, -0.2) * mm, "radius": 19.13 * mm});
            skPoint(sketch, "E254.first.point", {"position": v(-52.66, 17.51) * mm});
            skPoint(sketch, "E254.second.point", {"position": v(-27.36, -6.45) * mm});
            skPoint(sketch, "E254.third.point", {"position": v(-50.49, -18.64) * mm});
            skCircle(sketch, "E255", {"center": v(-45.33, -0.68) * mm, "radius": 22.86 * mm});
            skCircle(sketch, "E256", {"center": v(-44.46, -0.22) * mm, "radius": 23.4 * mm});
            skCircle(sketch, "E257", {"center": v(-44.41, -0.17) * mm, "radius": 26.64 * mm});
            skArc(sketch, "E258", {"start": v(-31.16, 22.94) * mm, "mid": v(-42.04, 42.88) * mm, "end": v(-55.17, 24.35) * mm});
            skArc(sketch, "E259", {"start": v(-34.63, 24.6) * mm, "mid": v(-42.8, 39.66) * mm, "end": v(-52.15, 25.32) * mm});
            skSolve(sketch);
        }
        {
            var Q0;
            {var subQ12=sQuery(id+"F0.wireOp",EDGE,"E146");Q0=makeQuery(id+"F0.imprint","IMPRINT",FACE,{"disambiguationData":[TD([[makeQuery(id+"F0.imprint","IMPRINT",EDGE,{"derivedFrom":subQ12}),-1.0]])]});}
            extrude(context, id + "F1", {"entities" : qUnion([Q0]), "depth" : 20 * mm, "offsetDistance" : 25 * mm});
        }
        {
            var Q0;
            {var subQ11=sQuery(id+"F0.wireOp",EDGE,"E154");Q0=makeQuery(id+"F0.imprint","IMPRINT",FACE,{"disambiguationData":[TD([[makeQuery(id+"F0.imprint","IMPRINT",EDGE,{"derivedFrom":subQ11}),-1.0]])]});}
            extrude(context, id + "F2", {"entities" : qUnion([Q0]), "depth" : 15 * mm, "offsetDistance" : 25 * mm});
        }
        {
            var Q0;
            {var subQ6=sQuery(id+"F0.wireOp",EDGE,"E0");Q0=makeQuery(id+"F0.imprint","IMPRINT",FACE,{"disambiguationData":[TD([[makeQuery(id+"F0.imprint","IMPRINT",EDGE,{"derivedFrom":subQ6}),-1.0]])]});}
            extrude(context, id + "F3", {"entities" : qUnion([Q0]), "operationType" : NewBodyOperationType.ADD, "depth" : 10 * mm, "offsetDistance" : 25 * mm});
        }
        {
            var Q0;
            {var subQ7=sQuery(id+"F0.wireOp",EDGE,"E117");Q0=makeQuery(id+"F0.imprint","IMPRINT",FACE,{"disambiguationData":[TD([[makeQuery(id+"F0.imprint","IMPRINT",EDGE,{"derivedFrom":subQ7}),-1.0]])]});}
            extrude(context, id + "F4", {"entities" : qUnion([Q0]), "depth" : 5 * mm, "offsetDistance" : 25 * mm});
        }
        {
            var Q0;
            {var subQ0=sQuery(id+"F0.wireOp",EDGE,"E258");var subQ1=sQuery(id+"F0.wireOp",EDGE,"E120");var subQ2=makeQuery(id+"F0.imprint","INTERSECT",VERTEX,{"derivedFrom":[subQ1,subQ0]});Q0=makeQuery(id+"F0.imprint","IMPRINT",FACE,{"disambiguationData":[TD([[makeQuery(id+"F0.imprint","IMPRINT",EDGE,{"disambiguationData":[TD([[subQ2,-1.0]])],"derivedFrom":subQ1}),1.0]])]});}
            extrude(context, id + "F5", {"entities" : qUnion([Q0]), "depth" : 5 * mm, "offsetDistance" : 25 * mm});
        }
        {
            var Q0;
            Q0=makeQuery(id+"F1.opExtrude","CAP_FACE",FACE,{"disambiguationData":[OSD([sQuery(id+"F0.wireOp",EDGE,"E146"),sQuery(id+"F0.wireOp",EDGE,"E147"),sQuery(id+"F0.wireOp",EDGE,"E148"),sQuery(id+"F0.wireOp",EDGE,"E149"),sQuery(id+"F0.wireOp",EDGE,"E151"),sQuery(id+"F0.wireOp",EDGE,"E252"),sQuery(id+"F0.wireOp",EDGE,"E253")])],"isStart":false});
            var sketch = newSketch(context, id + "F6", { "sketchPlane" : qUnion([Q0])});
            skText(sketch, "E260", { "text": "F", "fontName": "OpenSans-Bold.ttf"});
            skText(sketch, "E261", { "text": "G", "fontName": "OpenSans-Regular.ttf"});
            skCircle(sketch, "E262", {"center": v(-37.24, 8.14) * mm, "radius": 1.64 * mm});
            const initialGuessF6  = {"E260": [-0.0571, -0.00576, 1, 0, 0.01112], "E261": [-0.04697, -0.00576, 1, 0, 0.01112]};
            skSetInitialGuess(sketch, initialGuessF6);
            skSolve(sketch);
        }
        {
            var Q0;
            Q0 = qSketchRegion(id + "F6", true);
            extrude(context, id + "F7", {"entities" : qUnion([Q0]), "operationType" : NewBodyOperationType.ADD, "depth" : 3 * mm, "offsetDistance" : 25 * mm});
        }
        {
            var Q0;
            Q0=qCreatedBy(makeId("Top.planeOp"),FACE);
            var sketch = newSketch(context, id + "F8", { "sketchPlane" : qUnion([Q0])});
            skCircle(sketch, "E263", {"center": v(-44.54, -0.29) * mm, "radius": 25.65 * mm});
            skPoint(sketch, "E263.first.point", {"position": v(-69.58, -5.9) * mm});
            skPoint(sketch, "E263.second.point", {"position": v(-20.3, -8.69) * mm});
            skPoint(sketch, "E263.third.point", {"position": v(-46.85, 25.26) * mm});
            skSolve(sketch);
        }
        {
            var Q0;
            Q0=makeQuery(id+"F8.imprint","IMPRINT",FACE,{"disambiguationData":[TD([[makeQuery(id+"F8.imprint","IMPRINT",EDGE,{"derivedFrom":sQuery(id+"F8.wireOp",EDGE,"E263")}),1.0]])]});
            extrude(context, id + "F9", {"entities" : qUnion([Q0]), "depth" : 2 * mm, "offsetDistance" : 25 * mm});
        }
        {
            var Q0;
            Q0=makeQuery(id+"F5.opExtrude","CAP_EDGE",EDGE,{"disambiguationData":[OSD([sQuery(id+"F0.wireOp",EDGE,"E259")])],"isStart":true});
            var Q1;
            Q1=makeQuery(id+"F5.opExtrude","CAP_EDGE",EDGE,{"disambiguationData":[OSD([sQuery(id+"F0.wireOp",EDGE,"E259")])],"isStart":false});
            var Q2;
            Q2=makeQuery(id+"F5.opExtrude","CAP_EDGE",EDGE,{"disambiguationData":[OSD([sQuery(id+"F0.wireOp",EDGE,"E258")])],"isStart":false});
            var Q3;
            Q3=makeQuery(id+"F5.opExtrude","CAP_EDGE",EDGE,{"disambiguationData":[OSD([sQuery(id+"F0.wireOp",EDGE,"E258")])],"isStart":true});
            fillet(context, id + "F10", {"entities" : qUnion([Q0, Q1, Q2, Q3]), "radius" : 1 * mm, "tangentPropagation" : true, "allowEdgeOverflow" : false});
        }
    });
